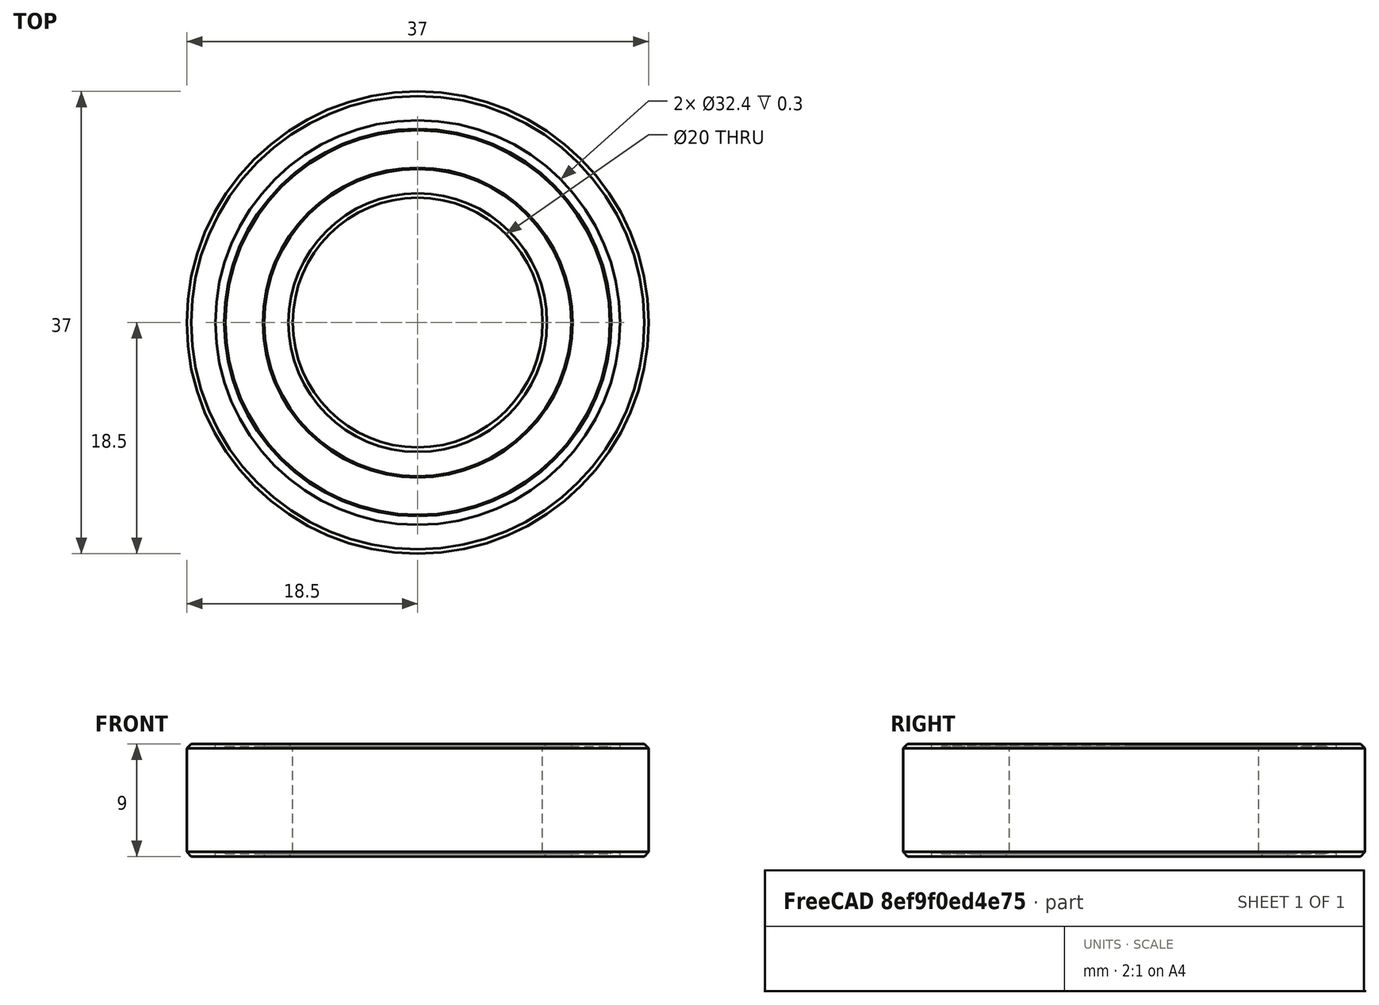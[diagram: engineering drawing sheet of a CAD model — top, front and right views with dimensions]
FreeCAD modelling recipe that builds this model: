
FCSTD DOCUMENT  (FreeCAD 0.20R28647 (Git))
Label: bearing
License: All rights reserved
LicenseURL: http://en.wikipedia.org/wiki/All_rights_reserved
objects: App::DocumentObjectGroup×3, PartDesign::CoordinateSystem×3, App::FeaturePython×1, Sketcher::SketchObject×1, PartDesign::Revolution×1, PartDesign::Body×1, App::Part×1
note: 7 computed .brp shape members not serialized (recipe doc carries the construction recipe); baked Part::Feature solids carry a one-line shape summary decoded from their .brp

FEATURE [App::DocumentObjectGroup] Parts
FEATURE [PartDesign::CoordinateSystem] LCS_Origin
  AttacherType = Attacher::AttachEngine3D
  MapMode = 2
  Support = -> [X_Axis]
FEATURE [App::FeaturePython] Variables  # WARN: FeaturePython — macro-defined, semantics opaque (R4)
  Type = App::PropertyContainer
FEATURE [App::DocumentObjectGroup] Constraints
FEATURE [App::DocumentObjectGroup] Configurations
FEATURE [Sketcher::SketchObject] Sketch
  FullyConstrained = true
  MapMode = 5
  Placement = pos=(0,0,0) rot=(1,0,0;1.5708rad)
  Support = -> [XZ_Plane001]
  sketch-geometry (22):
    g0: LineSegment StartX=-18.5 StartY=4.14645 StartZ=0 EndX=-18.5 EndY=-4.14645 EndZ=0
    g1: LineSegment StartX=-18.5 StartY=-4.14645 StartZ=0 EndX=-18.1464 EndY=-4.5 EndZ=0
    g2: LineSegment StartX=-18.1464 StartY=-4.5 StartZ=0 EndX=-16.2 EndY=-4.5 EndZ=0
    g3: LineSegment StartX=-16.2 StartY=-4.5 StartZ=0 EndX=-16.2 EndY=-4.2 EndZ=0
    g4: LineSegment StartX=-15.4 StartY=-4.3 StartZ=0 EndX=-12.4 EndY=-4.3 EndZ=0
    g5: LineSegment StartX=-12.4 StartY=-4.3 StartZ=0 EndX=-12.3 EndY=-4.2 EndZ=0
    g6: LineSegment StartX=-12.3 StartY=-4.2 StartZ=0 EndX=-12.3 EndY=-4.5 EndZ=0
    g7: LineSegment StartX=-12.3 StartY=-4.5 StartZ=0 EndX=-10.3536 EndY=-4.5 EndZ=0
    g8: LineSegment StartX=-10.3536 StartY=-4.5 StartZ=0 EndX=-10 EndY=-4.14645 EndZ=0
    g9: LineSegment StartX=-10 StartY=-4.14645 StartZ=0 EndX=-10 EndY=4.14645 EndZ=0
    g10: LineSegment StartX=-10 StartY=4.14645 StartZ=0 EndX=-10.3536 EndY=4.5 EndZ=0
    g11: LineSegment StartX=-10.3536 StartY=4.5 StartZ=0 EndX=-12.3 EndY=4.5 EndZ=0
    g12: LineSegment StartX=-12.3 StartY=4.5 StartZ=0 EndX=-12.3 EndY=4.2 EndZ=0
    g13: LineSegment StartX=-12.3 StartY=4.2 StartZ=0 EndX=-12.4 EndY=4.3 EndZ=0
    g14: LineSegment StartX=-12.4 StartY=4.3 StartZ=0 EndX=-15.4 EndY=4.3 EndZ=0
    g15: LineSegment StartX=-15.4 StartY=4.3 StartZ=0 EndX=-15.5 EndY=4.2 EndZ=0
    g16: LineSegment StartX=-15.5 StartY=4.2 StartZ=0 EndX=-16.2 EndY=4.2 EndZ=0
    g17: LineSegment StartX=-16.2 StartY=4.2 StartZ=0 EndX=-16.2 EndY=4.5 EndZ=0
    g18: LineSegment StartX=-16.2 StartY=4.5 StartZ=0 EndX=-18.1464 EndY=4.5 EndZ=0
    g19: LineSegment StartX=-18.1464 StartY=4.5 StartZ=0 EndX=-18.5 EndY=4.14645 EndZ=0
    g20: LineSegment StartX=-15.4 StartY=-4.3 StartZ=0 EndX=-15.5 EndY=-4.2 EndZ=0
    g21: LineSegment StartX=-15.5 StartY=-4.2 StartZ=0 EndX=-16.2 EndY=-4.2 EndZ=0
  constraints (61):
    c: Vertical(g0)
    c: Coincident(g0,g1)
    c: Coincident(g1,g2)
    c: Horizontal(g2)
    c: Coincident(g2,g3)
    c: Coincident(g4,g5)
    c: Coincident(g5,g6)
    c: Coincident(g6,g7)
    c: Coincident(g7,g8)
    c: Coincident(g8,g9)
    c: Coincident(g9,g10)
    c: Coincident(g10,g11)
    c: Horizontal(g11)
    c: Coincident(g11,g12)
    c: Vertical(g12)
    c: Coincident(g12,g13)
    c: Coincident(g13,g14)
    c: Horizontal(g14)
    c: Coincident(g14,g15)
    c: Coincident(g15,g16)
    c: Horizontal(g16)
    c: Coincident(g16,g17)
    c: Vertical(g17)
    c: Coincident(g17,g18)
    c: Horizontal(g18)
    c: Coincident(g18,g19)
    c: Coincident(g19,g0)
    c: Coincident(g4,g20)
    c: Coincident(g20,g21)
    c: Coincident(g21,g3)
    c: Vertical(g3)
    c: Horizontal(g21)
    c: Horizontal(g4)
    c: Vertical(g6)
    c: Horizontal(g7)
    c: Horizontal(g11,g17)
    c: Symmetric(g8,g9,g-1)
    c: Symmetric(g10,g7,g-1)
    c: Equal(g7,g11)
    c: Symmetric(g13,g4,g-1)
    c: Equal(g6,g12)
    c: Angle(g8) = 0.785398
    c: Parallel(g8,g19)
    c: Parallel(g15,g5)
    c: Parallel(g5,g8)
    c: Parallel(g13,g20)
    c: Parallel(g20,g1)
    c: Equal(g2,g18)
    c: Symmetric(g20,g15,g-1)
    c: Equal(g12,g17)
    c: Symmetric(g18,g1,g-1)
    c: DistanceY(g7,g10) = 9
    c: DistanceX(g8) = -10
    c: Distance(g8) = 0.5
    c: DistanceY(g6,g4) = 0.2
    c: Equal(g1,g8)
    c: Equal(g7,g2)
    c: DistanceY(g6,g6) = 0.3
    c: DistanceX(g0) = -18.5
    c: DistanceX(g4,g4) = 3
    c: DistanceX(g21,g21) = 0.7
FEATURE [PartDesign::Revolution] Revolution
  Angle = 360
  Axis = (0,-2e-16,1)
  Base = (0,0,0)
  Placement = pos=(0,0,0) rot=(1,0,0;1.5708rad)
  Profile = -> Sketch
  ReferenceAxis = -> Sketch [V_Axis]
FEATURE [PartDesign::Body] Body  label="BallBearing 37x20x9"
  Group = -> [Sketch,Revolution]
  Origin = -> Origin001
  Tip = -> Revolution
FEATURE [PartDesign::CoordinateSystem] LCS_1
  AttacherType = Attacher::AttachEngine3D
  MapMode = 11
  Placement = pos=(0,-1e-15,-4.5) rot=(0,0,-1;1.5708rad)
  Support = -> [Revolution]
FEATURE [PartDesign::CoordinateSystem] LCS_2
  AttacherType = Attacher::AttachEngine3D
  MapMode = 11
  Placement = pos=(0,1e-15,4.5) rot=(0,0,-1;1.5708rad)
  Support = -> [Revolution]
FEATURE [App::Part] Assembly  label="asm_Bearing 37x20x9"
  AssemblyType = Part::Link
  Group = -> [LCS_Origin,Variables,Constraints,Configurations,Body,LCS_1,LCS_2]
  LabelDocUser = bearing
  LabelPartUser = asm_Bearing 37x20x9
  Origin = -> Origin
  ShapeVolumeUser = 9.0 mm x 37.0 mm x 37.0 mm
  Type = Assembly
